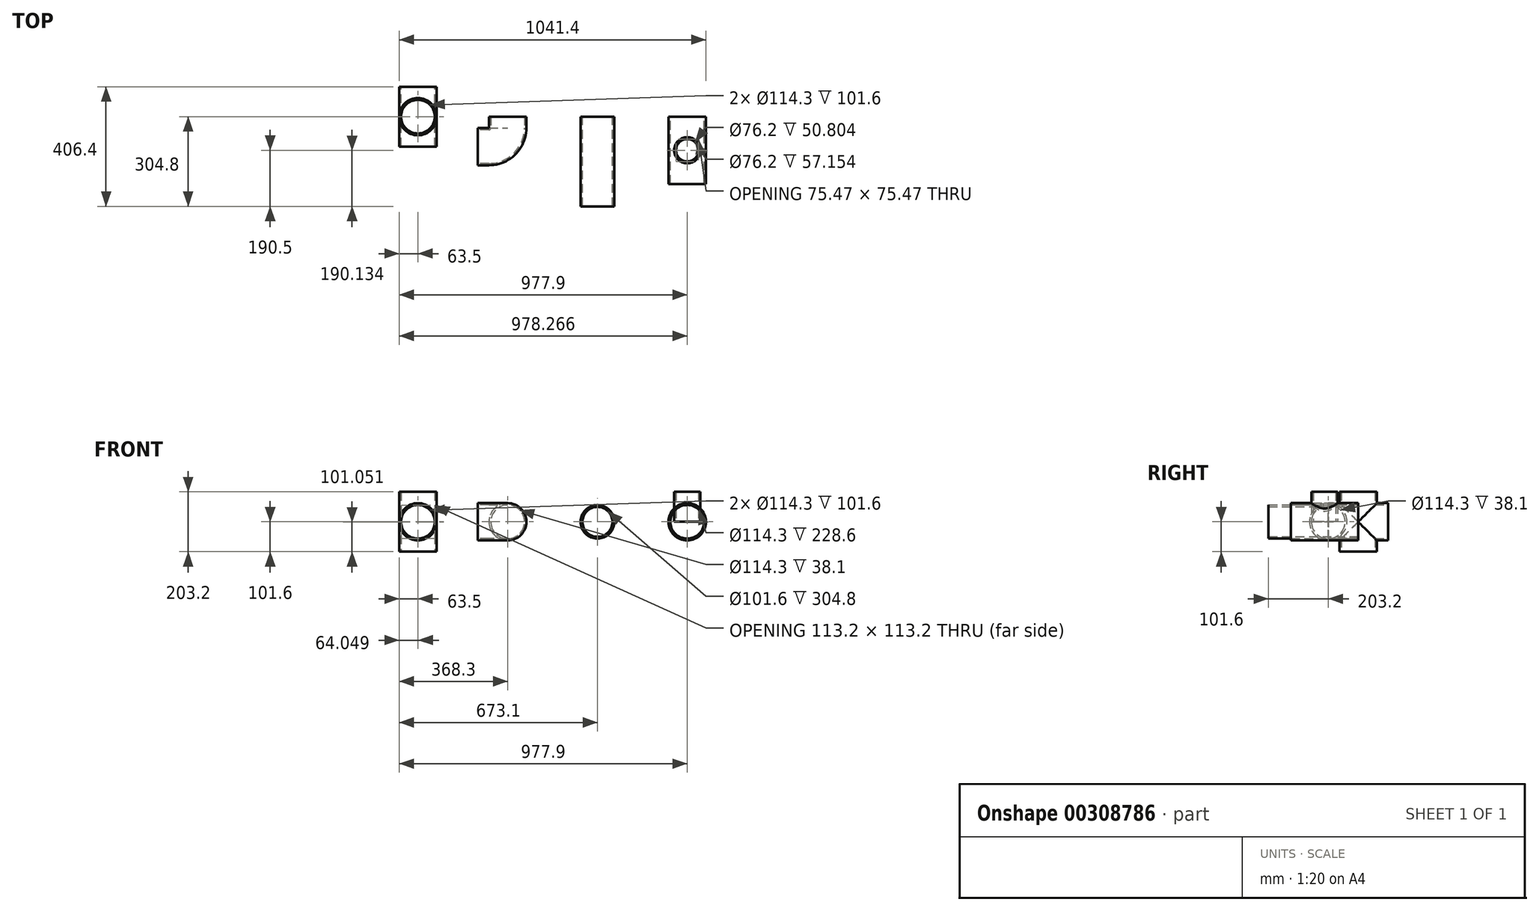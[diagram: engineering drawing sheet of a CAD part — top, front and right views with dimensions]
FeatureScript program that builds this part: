
annotation { "Feature Type Name" : "Feature", "Feature Type Description" : "" }
export const myFeature = defineFeature(function(context is Context, id is Id, definition is map)
    precondition{}
    {
        {
            var Q0;
            Q0=qCreatedBy(makeId("Front.planeOp"),FACE);
            var sketch = newSketch(context, id + "F0", { "sketchPlane" : qUnion([Q0])});
            skCircle(sketch, "E0", {"center": v(0, 0) * mm, "radius": 50.8 * mm});
            skCircle(sketch, "E1", {"center": v(0, 0) * mm, "radius": 57.15 * mm});
            skSolve(sketch);
        }
        {
            var Q0;
            Q0=makeQuery(id+"F0.imprint","IMPRINT",FACE,{"disambiguationData":[TD([[makeQuery(id+"F0.imprint","IMPRINT",EDGE,{"derivedFrom":sQuery(id+"F0.wireOp",EDGE,"E0")}),-1.0]])]});
            extrude(context, id + "F1", {"entities" : qUnion([Q0]), "depth" : 304.8 * mm});
        }
        {
            var Q0;
            Q0=qCreatedBy(makeId("Front.planeOp"),FACE);
            var sketch = newSketch(context, id + "F2", { "sketchPlane" : qUnion([Q0])});
            skCircle(sketch, "E2", {"center": v(304.8, 0) * mm, "radius": 57.15 * mm});
            skCircle(sketch, "E3", {"center": v(304.8, 0) * mm, "radius": 63.5 * mm});
            skSolve(sketch);
        }
        {
            var Q0;
            Q0=makeQuery(id+"F2.imprint","IMPRINT",FACE,{"disambiguationData":[TD([[makeQuery(id+"F2.imprint","IMPRINT",EDGE,{"derivedFrom":sQuery(id+"F2.wireOp",EDGE,"E2")}),-1.0]])]});
            extrude(context, id + "F3", {"entities" : qUnion([Q0]), "depth" : 228.6 * mm});
        }
        {
            var Q0;
            Q0=qCreatedBy(makeId("Top.planeOp"),FACE);
            var sketch = newSketch(context, id + "F4", { "sketchPlane" : qUnion([Q0])});
            skCircle(sketch, "E4", {"center": v(304.8, -114.3) * mm, "radius": 44.45 * mm});
            skCircle(sketch, "E5", {"center": v(304.8, -114.3) * mm, "radius": 38.1 * mm});
            skSolve(sketch);
        }
        {
            var Q0;
            Q0 = qSketchRegion(id + "F4", true);
            extrude(context, id + "F5", {"entities" : qUnion([Q0]), "operationType" : NewBodyOperationType.ADD, "depth" : 101.6 * mm});
        }
        {
            var Q0;
            Q0=qCreatedBy(makeId("Front.planeOp"),FACE);
            var sketch = newSketch(context, id + "F6", { "sketchPlane" : qUnion([Q0])});
            skCircle(sketch, "E6", {"center": v(-304.8, 0) * mm, "radius": 57.15 * mm});
            skCircle(sketch, "E7", {"center": v(-304.8, 0) * mm, "radius": 63.5 * mm});
            skSolve(sketch);
        }
        {
            var Q0;
            Q0=qCreatedBy(makeId("Top.planeOp"),FACE);
            var sketch = newSketch(context, id + "F7", { "sketchPlane" : qUnion([Q0])});
            skLineSegment(sketch, "E8", {"start": v(-304.8, 0) * mm, "end": v(-304.8, -38.1) * mm});
            skLineSegment(sketch, "E9", {"start": v(-368.3, -101.6) * mm, "end": v(-406.4, -101.6) * mm});
            skPoint(sketch, "E10.visualSharp", {"position": v(-304.8, -101.6) * mm});
            skArc(sketch, "E10.filletArc", {"start": v(-368.3, -101.6) * mm, "mid": v(-323.4, -83) * mm, "end": v(-304.8, -38.1) * mm});
            skSolve(sketch);
        }
        {
            var Q0;
            Q0=makeQuery(id+"F6.imprint","IMPRINT",FACE,{"disambiguationData":[TD([[makeQuery(id+"F6.imprint","IMPRINT",EDGE,{"derivedFrom":sQuery(id+"F6.wireOp",EDGE,"E6")}),-1.0]])]});
            var Q1;
            Q1 = qConstructionFilter(qBodyType(qCreatedBy(id + "F7" ,EDGE), BodyType.WIRE), ConstructionObject.NO);
            sweep(context, id + "F8", {"profiles" : qUnion([Q0]), "path" : qUnion([Q1])});
        }
        {
            var Q0;
            Q0=qCreatedBy(makeId("Front.planeOp"),FACE);
            var sketch = newSketch(context, id + "F9", { "sketchPlane" : qUnion([Q0])});
            skCircle(sketch, "E11", {"center": v(-609.6, 0) * mm, "radius": 57.15 * mm});
            skCircle(sketch, "E12", {"center": v(-609.6, 0) * mm, "radius": 63.5 * mm});
            skSolve(sketch);
        }
        {
            var Q0;
            Q0=makeQuery(id+"F9.imprint","IMPRINT",FACE,{"disambiguationData":[TD([[makeQuery(id+"F9.imprint","IMPRINT",EDGE,{"derivedFrom":sQuery(id+"F9.wireOp",EDGE,"E11")}),-1.0]])]});
            extrude(context, id + "F10", {"entities" : qUnion([Q0]), "endBound" : BoundingType.SYMMETRIC, "depth" : 203.2 * mm});
        }
        {
            var Q0;
            Q0=qCreatedBy(makeId("Top.planeOp"),FACE);
            var sketch = newSketch(context, id + "F11", { "sketchPlane" : qUnion([Q0])});
            skCircle(sketch, "E13", {"center": v(-609.6, 0) * mm, "radius": 57.15 * mm});
            skCircle(sketch, "E14", {"center": v(-609.6, 0) * mm, "radius": 63.5 * mm});
            skSolve(sketch);
        }
        {
            var Q0;
            Q0 = qSketchRegion(id + "F11", true);
            extrude(context, id + "F12", {"entities" : qUnion([Q0]), "operationType" : NewBodyOperationType.ADD, "endBound" : BoundingType.SYMMETRIC, "depth" : 203.2 * mm});
        }
        {
            var Q0;
            Q0=makeQuery(id+"F11.imprint","IMPRINT",FACE,{"disambiguationData":[TD([[makeQuery(id+"F11.imprint","IMPRINT",EDGE,{"derivedFrom":sQuery(id+"F11.wireOp",EDGE,"E13")}),1.0]])]});
            extrude(context, id + "F13", {"entities" : qUnion([Q0]), "operationType" : NewBodyOperationType.REMOVE, "endBound" : BoundingType.SYMMETRIC, "oppositeDirection" : true, "depth" : 203.2 * mm});
        }
        {
            var Q0;
            Q0=makeQuery(id+"F9.imprint","IMPRINT",FACE,{"disambiguationData":[TD([[makeQuery(id+"F9.imprint","IMPRINT",EDGE,{"derivedFrom":sQuery(id+"F9.wireOp",EDGE,"E11")}),1.0]])]});
            var Q1;
            Q1=sQuery(id+"F9.wireOp",EDGE,"E11");
            extrude(context, id + "F14", {"entities" : qUnion([Q0]), "operationType" : NewBodyOperationType.REMOVE, "surfaceEntities" : qUnion([Q1]), "endBound" : BoundingType.SYMMETRIC, "depth" : 203.2 * mm});
        }
    });
